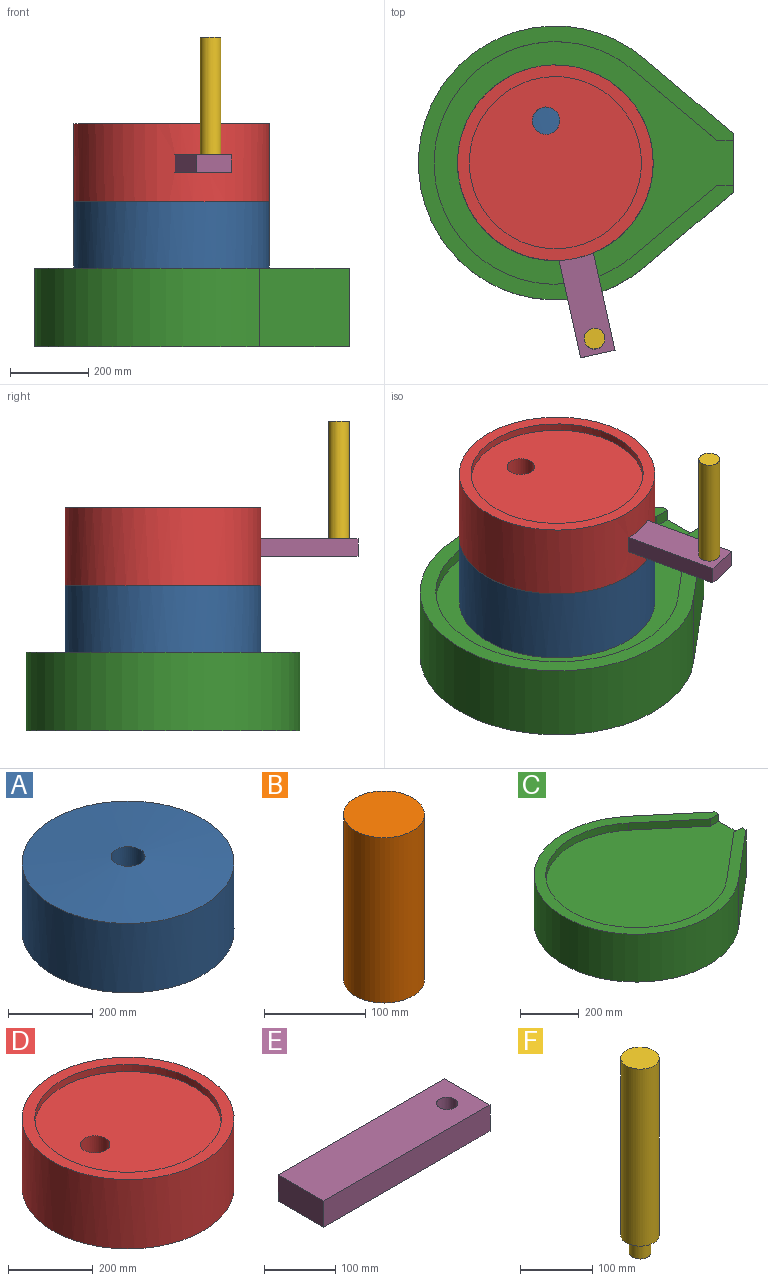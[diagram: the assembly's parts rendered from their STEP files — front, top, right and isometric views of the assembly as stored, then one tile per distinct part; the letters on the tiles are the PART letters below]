
ASSEMBLY  parts=6 mates=5
PART A: 5 faces, bbox 500x500x216.8 mm
  f0: cone r=250mm half-angle=85.4deg, axis (0,0,-1), area 191934.2mm2, adj f1,f3
  f1: cylinder r=250mm len=500mm, axis (0,0,-1), area 314159.3mm2, adj f0,f2
  f2: plane 500x500mm, normal (0,0,-1), area 196349.5mm2, adj f1
  f3: cylinder r=40mm len=116.8mm, axis (0,0,-1), area 29355mm2, adj f0,f4
  f4: plane 80x80mm, normal (0,0,1), area 5026.5mm2, adj f3
PART B: 3 faces, bbox 80x80x200 mm
  f0: cylinder r=40mm len=200mm, axis (0,0,-1), area 50265.5mm2, adj f1,f2
  f1: plane 80x80mm, normal (0,0,1), area 5026.5mm2, adj f0
  f2: plane 80x80mm, normal (0,0,-1), area 5026.5mm2, adj f0
PART C: 12 faces, bbox 804.8x700x200 mm
  f0: plane 200x150mm, normal (1,0,0), area 26618.2mm2, adj f1,f3,f4,f5,f6,f10,f11
  f1: plane 804.84x700mm, normal (0,0,1), area 83915.9mm2, adj f0,f2,f3,f4,f6,f7,f8,f9
  f2: cylinder r=350mm len=700mm, axis (0,0,-1), area 317735.9mm2, adj f1,f3,f4,f5
  f3: plane 229.7x200mm, normal (0.64,-0.77,0), area 60000mm2, adj f0,f1,f2,f5
  f4: plane 229.7x200mm, normal (0.64,0.77,0), area 60000mm2, adj f0,f1,f2,f5
  f5: plane 804.84x700mm, normal (0,0,-1), area 417131.5mm2, adj f0,f2,f3,f4
  f6: plane 40x30mm, normal (0,-1,0), area 1200mm2, adj f0,f1,f7,f11
  f7: plane 215.43x180.99mm, normal (-0.64,-0.77,0), area 8440.9mm2, adj f1,f6,f8,f11
  f8: cylinder r=310mm len=620mm, axis (0,0,1), area 42213.5mm2, adj f1,f7,f9,f11
  f9: plane 215.43x180.99mm, normal (-0.64,0.77,0), area 8440.9mm2, adj f1,f8,f10,f11
  f10: plane 40x30mm, normal (0,1,0), area 1200mm2, adj f0,f1,f9,f11
  f11: plane 764.84x620mm, normal (0,0,1), area 333215.6mm2, adj f0,f6,f7,f8,f9,f10
PART D: 13 faces, bbox 500x500x200 mm
  f0: cylinder r=250mm len=500mm, axis (0,0,-1), area 310087.1mm2, adj f1,f2,f8,f9,f10,f11
  f1: cone r=250mm half-angle=85.4deg, axis (0,0,-1), area 188073.4mm2, adj f0,f3,f7
  f2: plane 500x500mm, normal (0,0,1), area 44296.5mm2, adj f0,f5
  f3: cylinder r=40mm len=83.2mm, axis (0,0,-1), area 20910.4mm2, adj f1,f4
  f4: plane 80x80mm, normal (0,0,-1), area 5026.5mm2, adj f3
  f5: cylinder r=220mm len=440mm, axis (0,0,1), area 27646mm2, adj f2,f6
  f6: plane 440x440mm, normal (0,0,1), area 148204.6mm2, adj f5,f7
  f7: cylinder r=35mm len=171.6mm, axis (0,0,1), area 37170.4mm2, adj f1,f6
  f8: plane 90x79.17mm, normal (0,0,-1), area 7002.7mm2, adj f0,f9,f11,f12
  f9: plane 75.08x45mm, normal (0,1,0), area 3378.7mm2, adj f0,f8,f10,f12
  f10: plane 90x79.17mm, normal (0,0,1), area 7002.7mm2, adj f0,f9,f11,f12
  f11: plane 75.08x45mm, normal (0,-1,0), area 3378.7mm2, adj f0,f8,f10,f12
  f12: plane 90x45mm, normal (1,0,0), area 4050mm2, adj f8,f9,f10,f11
PART E: 8 faces, bbox 330x90x45 mm
  f0: plane 330x90mm, normal (0,0,1), area 28993.1mm2, adj f1,f3,f4,f5,f6
  f1: plane 330x45mm, normal (0,-1,0), area 14850mm2, adj f0,f2,f4,f5
  f2: plane 330x90mm, normal (0,0,-1), area 29700mm2, adj f1,f3,f4,f5
  f3: plane 330x45mm, normal (0,1,0), area 14850mm2, adj f0,f2,f4,f5
  f4: plane 90x45mm, normal (-1,0,0), area 4050mm2, adj f0,f1,f2,f3
  f5: plane 90x45mm, normal (1,0,0), area 4050mm2, adj f0,f1,f2,f3
  f6: cylinder r=15mm len=30mm, axis (0,0,1), area 2827.4mm2, adj f0,f7
  f7: plane 30x30mm, normal (0,0,1), area 706.9mm2, adj f6
PART F: 5 faces, bbox 53.1x53.1x330 mm
  f0: cylinder r=15mm len=30mm, axis (0,0,1), area 2827.4mm2, adj f1,f4
  f1: plane 30x30mm, normal (0,0,-1), area 706.9mm2, adj f0
  f2: cylinder r=26.57mm len=300mm, axis (0,0,-1), area 50083.7mm2, adj f3,f4
  f3: plane 53.14x53.14mm, normal (0,0,1), area 2217.9mm2, adj f2
  f4: plane 53.14x53.14mm, normal (0,0,-1), area 1511mm2, adj f0,f2
PLACE A at identity
PLACE B at identity
PLACE C at identity fixed
PLACE D rot(axis=(0,0,-1),77.5deg) t=(0,0,0)mm
PLACE E rot(axis=(0,0,-1),77.5deg) t=(0,0,0)mm
PLACE F rot(axis=(0,0,-1),77.5deg) t=(0,0,0)mm
MATE revolute D.f3 <-> B.f0  axis (0,0,-1) through (0,0,470)mm
MATE fastened A.f1 <-> C.f8  axis (0,0,-1) through (0,0,170)mm
MATE fastened F.f0 <-> E.f6  axis (0,0,-1) through (99.88,-449.88,460)mm
MATE fastened E.f4 <-> D.f12  axis (-0.22,0.98,0) through (37.03,-166.77,467.5)mm
MATE fastened A.f3 <-> B.f0  axis (0,0,1) through (0,0,270)mm
